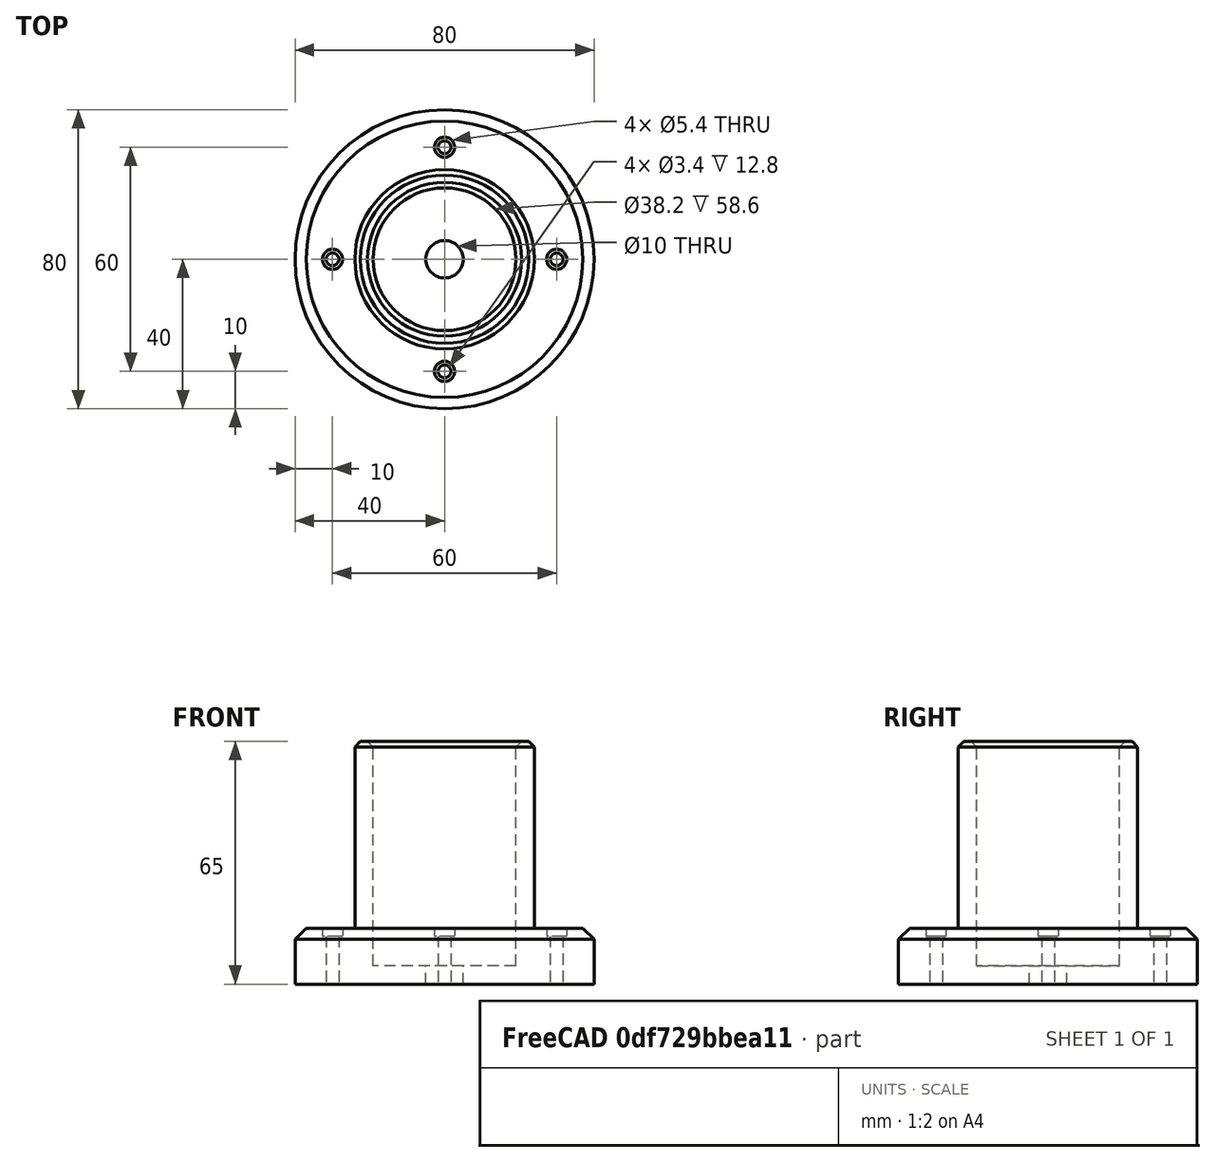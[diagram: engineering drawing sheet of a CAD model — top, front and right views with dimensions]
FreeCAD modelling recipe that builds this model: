
FCSTD DOCUMENT  (FreeCAD 0.19R24276 (Git))
Label: piezaPatxenker
License: All rights reserved
LicenseURL: http://en.wikipedia.org/wiki/All_rights_reserved
objects: TechDraw::DrawViewDimension×9, Part::Cylinder×4, Part::Feature×4, Part::Cut×3, Part::Chamfer×3, TechDraw::DrawProjGroupItem×3, Part::MultiFuse×2, TechDraw::DrawSVGTemplate×2, TechDraw::DrawViewPart×2, TechDraw::DrawPage×2, Part::Offset×1, TechDraw::DrawProjGroup×1, TechDraw::DrawViewAnnotation×1
note: 17 computed .brp shape members not serialized (recipe doc carries the construction recipe); baked Part::Feature solids carry a one-line shape summary decoded from their .brp

FEATURE [Part::Cylinder] Cylinder
  Angle = 360
  AttacherType = Attacher::AttachEngine3D
  Height = 15
  Radius = 40
FEATURE [Part::Feature] Part__Feature  label="Offset"
  Placement = pos=(0,30,13) rot=(0,0,1;0rad)
  shape: bbox 5.845 x 5.845 x 22.4 mm, 8 faces (baked)
FEATURE [Part::Feature] Part__Feature001  label="Offset001"
  Placement = pos=(0,-30,13) rot=(0,0,1;0rad)
  shape: bbox 5.845 x 5.845 x 22.4 mm, 8 faces (baked)
FEATURE [Part::Feature] Part__Feature002  label="Offset002"
  Placement = pos=(30,0,13) rot=(0,0,1;0rad)
  shape: bbox 5.845 x 5.845 x 22.4 mm, 8 faces (baked)
FEATURE [Part::Feature] Part__Feature003  label="Offset003"
  Placement = pos=(-30,0,13) rot=(0,0,1;0rad)
  shape: bbox 5.845 x 5.845 x 22.4 mm, 8 faces (baked)
FEATURE [Part::MultiFuse] Fusion
  Shapes = -> [Part__Feature,Part__Feature001,Part__Feature002,Part__Feature003]
FEATURE [Part::Cut] Cut
  Base = -> Cylinder
  Tool = -> Fusion
FEATURE [Part::Chamfer] Chamfer
  Base = -> Cut
  Edges = 1 edges r=3: [Edge1]
FEATURE [Part::Cylinder] Cylinder001
  Angle = 360
  AttacherType = Attacher::AttachEngine3D
  Height = 100
  Placement = pos=(0,0,5) rot=(0,0,1;0rad)
  Radius = 19
FEATURE [Part::Cylinder] Cylinder002
  Angle = 360
  AttacherType = Attacher::AttachEngine3D
  Height = 65
  Radius = 24
FEATURE [Part::MultiFuse] Fusion001
  Shapes = -> [Cylinder002,Chamfer]
FEATURE [Part::Offset] Offset  label="Offset004"
  Fill = false
  Intersection = false
  Join = 2
  Mode = 0
  SelfIntersection = false
  Source = -> Cylinder001
  Value = 0.1
FEATURE [Part::Cut] Cut001
  Base = -> Fusion001
  Tool = -> Offset
FEATURE [Part::Cylinder] Cylinder003
  Angle = 360
  AttacherType = Attacher::AttachEngine3D
  Height = 10
  Radius = 5
FEATURE [Part::Cut] Cut002
  Base = -> Cut001
  Tool = -> Cylinder003
FEATURE [Part::Chamfer] Chamfer001
  Base = -> Cut002
  Edges = 1 edges r=1.5: [Edge2]
FEATURE [Part::Chamfer] Chamfer002
  Base = -> Chamfer001
  Edges = 1 edges r=1.5: [Edge2]
FEATURE [TechDraw::DrawSVGTemplate] Template
  EditableTexts = Designed_by_Name=<owner>; Drawing_number=001; FC-Date=-; FC-SC=1:2; FC-SH=1/2; FC-Title=CoatRackPiece; Subtitle=Pieza Perchero; Weight=<250gr
  Height = 210
  Orientation = 1
  Width = 297
FEATURE [TechDraw::DrawSVGTemplate] Template001
  EditableTexts = Designed_by_Name=<owner>; Drawing_number=001; FC-Date=-; FC-SC=1/1; FC-SH=2/2; FC-Title=Coat Rack Piece; Subtitle=Pieza Perchero; Weight=<250gr
  Height = 210
  Orientation = 1
  Width = 297
FEATURE [TechDraw::DrawViewPart] View
  CoarseView = false
  Direction = (-0.531,-0.619,0.579)
  Focus = 100
  HardHidden = false
  IsoCount = 0
  IsoHidden = false
  IsoVisible = false
  LockPosition = false
  Perspective = false
  Rotation = 0
  ScaleType = 0
  SeamHidden = false
  SeamVisible = true
  SmoothHidden = false
  SmoothVisible = true
  Source = -> [Chamfer002]
  X = 207.331
  XDirection = (0.845,-0.336,0.416)
  Y = 135.779
FEATURE [TechDraw::DrawViewPart] View001
  CoarseView = false
  Direction = (-0.531,-0.619,0.579)
  Focus = 100
  HardHidden = false
  IsoCount = 0
  IsoHidden = false
  IsoVisible = false
  LockPosition = false
  Perspective = false
  Rotation = 0
  ScaleType = 0
  SeamHidden = false
  SeamVisible = true
  SmoothHidden = false
  SmoothVisible = true
  Source = -> [Chamfer002]
  X = 149.658
  XDirection = (0.845,-0.336,0.416)
  Y = 121.883
FEATURE [TechDraw::DrawProjGroupItem] ProjItem  label="Front"
  CoarseView = false
  Direction = (0,-1,0)
  Focus = 100
  HardHidden = false
  IsoCount = 0
  IsoHidden = false
  IsoVisible = false
  LockPosition = true
  Perspective = false
  Rotation = 0
  RotationVector = (1,0,0)
  Scale = 0.5
  ScaleType = 2
  SeamHidden = false
  SeamVisible = true
  SmoothHidden = false
  SmoothVisible = true
  Source = -> [Chamfer002]
  Type = 0
  X = 0
  XDirection = (1,0,0)
  Y = 0
FEATURE [TechDraw::DrawProjGroupItem] ProjItem001  label="Right"
  CoarseView = false
  Direction = (1,-1e-16,0)
  Focus = 100
  HardHidden = false
  IsoCount = 0
  IsoHidden = false
  IsoVisible = false
  LockPosition = false
  Perspective = false
  Rotation = 0
  RotationVector = (1,0,0)
  Scale = 0.5
  ScaleType = 2
  SeamHidden = false
  SeamVisible = true
  SmoothHidden = false
  SmoothVisible = true
  Source = -> [Chamfer002]
  Type = 2
  X = -55
  XDirection = (1e-16,1,0)
  Y = 0
FEATURE [TechDraw::DrawProjGroupItem] ProjItem002  label="Top"
  CoarseView = false
  Direction = (0,0,1)
  Focus = 100
  HardHidden = false
  IsoCount = 0
  IsoHidden = false
  IsoVisible = false
  LockPosition = false
  Perspective = false
  Rotation = 0
  RotationVector = (1,0,0)
  Scale = 0.5
  ScaleType = 2
  SeamHidden = false
  SeamVisible = true
  SmoothHidden = false
  SmoothVisible = true
  Source = -> [Chamfer002]
  Type = 4
  X = 0
  XDirection = (1,0,0)
  Y = -55
FEATURE [TechDraw::DrawProjGroup] ProjGroup
  Anchor = -> ProjItem
  AutoDistribute = true
  LockPosition = false
  ProjectionType = 0
  Rotation = 0
  Scale = 0.5
  ScaleType = 2
  Source = -> [Chamfer002]
  Views = -> [ProjItem,ProjItem001,ProjItem002]
  X = 110.708
  Y = 165.39
  spacingX = 15
  spacingY = 15
FEATURE [TechDraw::DrawViewDimension] Dimension
  Arbitrary = false
  ArbitraryTolerances = false
  EqualTolerance = true
  FormatSpec = %.2f
  FormatSpecOverTolerance = %+.2f
  FormatSpecUnderTolerance = %+.2f
  Inverted = false
  LockPosition = false
  MeasureType = 1
  OverTolerance = 0
  References2D = -> [ProjItem]
  Rotation = 0
  ScaleType = 0
  TheoreticalExact = false
  Type = 1
  UnderTolerance = 0
  X = 0.341759
  Y = -20.9645
FEATURE [TechDraw::DrawViewDimension] Dimension001
  Arbitrary = false
  ArbitraryTolerances = false
  EqualTolerance = true
  FormatSpec = %.2f
  FormatSpecOverTolerance = %+.2f
  FormatSpecUnderTolerance = %+.2f
  Inverted = false
  LockPosition = false
  MeasureType = 1
  OverTolerance = 0
  References2D = -> [ProjItem]
  Rotation = 0
  ScaleType = 0
  TheoreticalExact = false
  Type = 2
  UnderTolerance = 0
  X = 24.6813
  Y = 2.26406
FEATURE [TechDraw::DrawViewDimension] Dimension002
  Arbitrary = false
  ArbitraryTolerances = false
  EqualTolerance = true
  FormatSpec = ⌀%.2f
  FormatSpecOverTolerance = %+.2f
  FormatSpecUnderTolerance = %+.2f
  Inverted = false
  LockPosition = false
  MeasureType = 1
  OverTolerance = 0
  References2D = -> [ProjItem002]
  Rotation = 0
  ScaleType = 0
  TheoreticalExact = false
  Type = 5
  UnderTolerance = 0
  X = -49.0604
  Y = -9.91646
FEATURE [TechDraw::DrawViewDimension] Dimension003
  Arbitrary = false
  ArbitraryTolerances = false
  EqualTolerance = true
  FormatSpec = ⌀%.2f
  FormatSpecOverTolerance = %+.2f
  FormatSpecUnderTolerance = %+.2f
  Inverted = false
  LockPosition = false
  MeasureType = 1
  OverTolerance = 0
  References2D = -> [ProjItem002]
  Rotation = 0
  ScaleType = 0
  TheoreticalExact = false
  Type = 5
  UnderTolerance = 0
  X = -43.0583
  Y = 20.6158
FEATURE [TechDraw::DrawPage] Page  label="Vistas"
  KeepUpdated = true
  NextBalloonIndex = 1
  ProjectionType = 0
  Template = -> Template
  Views = -> [View,ProjGroup,Dimension,Dimension001,Dimension002,Dimension003]
FEATURE [TechDraw::DrawViewDimension] Dimension004
  Arbitrary = false
  ArbitraryTolerances = false
  EqualTolerance = true
  FormatSpec = %.2f
  FormatSpecOverTolerance = %+.2f
  FormatSpecUnderTolerance = %+.2f
  Inverted = false
  LockPosition = false
  MeasureType = 1
  OverTolerance = 0
  References2D = -> [View001]
  Rotation = 0
  ScaleType = 0
  TheoreticalExact = false
  Type = 0
  UnderTolerance = 0
  X = -73.2868
  Y = 5.32738
FEATURE [TechDraw::DrawViewDimension] Dimension005
  Arbitrary = false
  ArbitraryTolerances = false
  EqualTolerance = true
  FormatSpec = ⌀%.2f
  FormatSpecOverTolerance = %+.2f
  FormatSpecUnderTolerance = %+.2f
  Inverted = false
  LockPosition = false
  MeasureType = 1
  OverTolerance = 0
  References2D = -> [View001]
  Rotation = 0
  ScaleType = 0
  TheoreticalExact = false
  Type = 5
  UnderTolerance = 0
  X = 0.434932
  Y = -3.26199
FEATURE [TechDraw::DrawViewDimension] Dimension006
  Arbitrary = false
  ArbitraryTolerances = false
  EqualTolerance = true
  FormatSpec = ⌀%.2f
  FormatSpecOverTolerance = %+.2f
  FormatSpecUnderTolerance = %+.2f
  Inverted = false
  LockPosition = false
  MeasureType = 1
  OverTolerance = 0
  References2D = -> [View001]
  Rotation = 0
  ScaleType = 0
  TheoreticalExact = false
  Type = 5
  UnderTolerance = 0
  X = -20.768
  Y = -21.7466
FEATURE [TechDraw::DrawViewDimension] Dimension007
  Arbitrary = false
  ArbitraryTolerances = false
  EqualTolerance = true
  FormatSpec = %.2f
  FormatSpecOverTolerance = %+.2f
  FormatSpecUnderTolerance = %+.2f
  Inverted = false
  LockPosition = false
  MeasureType = 1
  OverTolerance = 0
  References2D = -> [View001]
  Rotation = 0
  ScaleType = 0
  TheoreticalExact = false
  Type = 0
  UnderTolerance = 0
  X = 76.8478
  Y = 25.9036
FEATURE [TechDraw::DrawViewDimension] Dimension008
  Arbitrary = false
  ArbitraryTolerances = false
  EqualTolerance = true
  FormatSpec = %.2f
  FormatSpecOverTolerance = %+.2f
  FormatSpecUnderTolerance = %+.2f
  Inverted = false
  LockPosition = false
  MeasureType = 1
  OverTolerance = 0
  References2D = -> [View001]
  Rotation = 0
  ScaleType = 0
  TheoreticalExact = false
  Type = 0
  UnderTolerance = 0
  X = 60.4359
  Y = -5.75646
FEATURE [TechDraw::DrawViewAnnotation] Annotation
  Font = osifont
  LineSpace = 80
  LockPosition = false
  MaxWidth = -1
  Rotation = 0
  ScaleType = 0
  Text = Aproximate measurements: | Check with 3D piece
  TextSize = 5
  TextStyle = 0
  X = 69.3
  Y = 67.8
FEATURE [TechDraw::DrawPage] Page001  label="Cotas"
  KeepUpdated = true
  NextBalloonIndex = 1
  ProjectionType = 0
  Template = -> Template001
  Views = -> [View001,Dimension004,Dimension005,Dimension006,Dimension007,Dimension008,Annotation]
